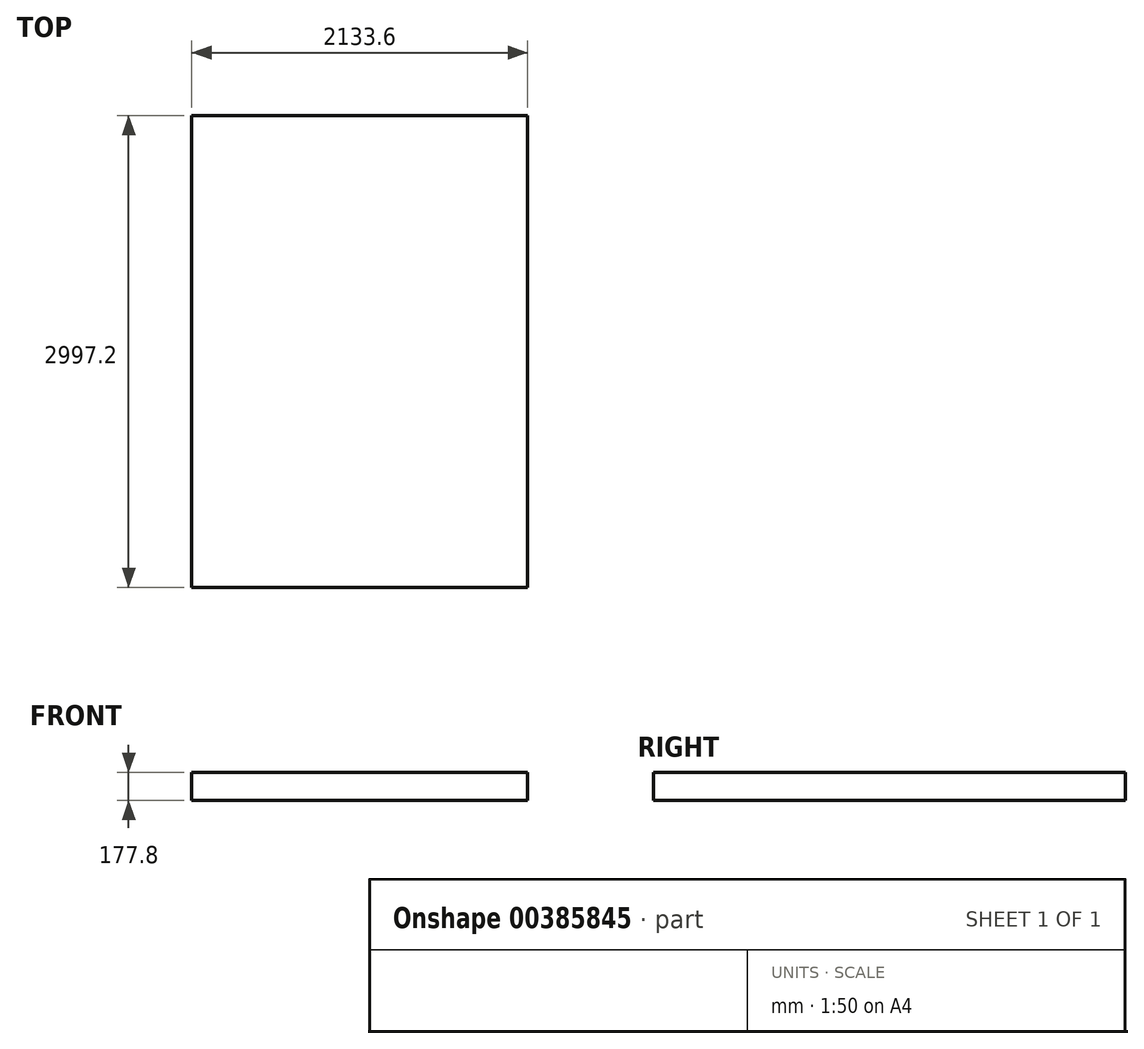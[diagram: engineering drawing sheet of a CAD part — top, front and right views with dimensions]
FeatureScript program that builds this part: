
annotation { "Feature Type Name" : "Feature", "Feature Type Description" : "" }
export const myFeature = defineFeature(function(context is Context, id is Id, definition is map)
    precondition{}
    {
        {
            var Q0;
            Q0=qCreatedBy(makeId("Top.planeOp"),FACE);
            var sketch = newSketch(context, id + "F0", { "sketchPlane" : qUnion([Q0])});
            skLineSegment(sketch, "E0.bottom", {"start": v(1066.8, -344.34) * mm, "end": v(-1066.8, -344.34) * mm});
            skLineSegment(sketch, "E0.top", {"start": v(1066.8, 2652.86) * mm, "end": v(-1066.8, 2652.86) * mm});
            skLineSegment(sketch, "E0.left", {"start": v(1066.8, -344.34) * mm, "end": v(1066.8, 2652.86) * mm});
            skLineSegment(sketch, "E0.right", {"start": v(-1066.8, -344.34) * mm, "end": v(-1066.8, 2652.86) * mm});
            skPoint(sketch, "E0.middle", {"position": v(0, 1154.26) * mm});
            skSolve(sketch);
        }
        {
            var Q0;
            Q0 = qSketchRegion(id + "F0", true);
            extrude(context, id + "F1", {"entities" : qUnion([Q0]), "depth" : 177.8 * mm});
        }
    });
